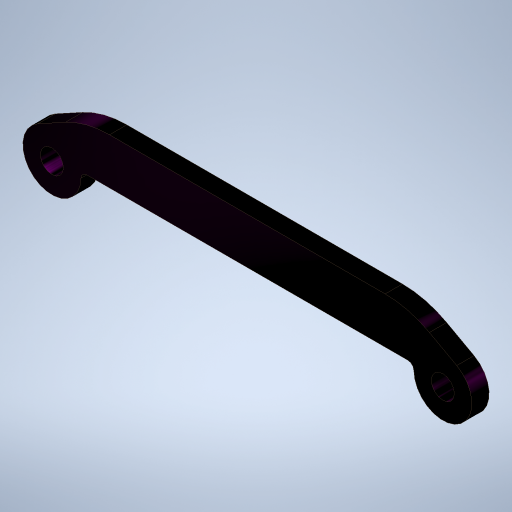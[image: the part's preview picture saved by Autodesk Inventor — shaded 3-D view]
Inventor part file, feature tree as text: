
AUTODESK INVENTOR PART (.ipt)
format: ipt  version: 2023.1 (Build 271208000, 208)  size: 269,312 bytes
history: native  units: in
note: dims shown in document units (in); Inventor stores cm internally (conversion verified against a paired STEP export)
features: fillet x2, extrude x1, sketch x1
ambient origin geometry x8: Origin, YZ Plane, XZ Plane, XY Plane, X Axis, Y Axis, Z Axis, Center Point
bodies: Solid1 (feature_tree)
feature tree (4):
  extrude  "Extrusion1"  Depth=0.032in
  fillet  "Fillet1"  Radius=0.188in
  fillet  "Fillet2"  Radius=0.25in
  sketch  "Sketch1"  dims[d0=0.315in d1=0.125in d2=0.188in d3=0.25in d4=1.75in d5=2.12in d6=0.0938in d7=0.0in d8=0.5in d9=0.032in]
